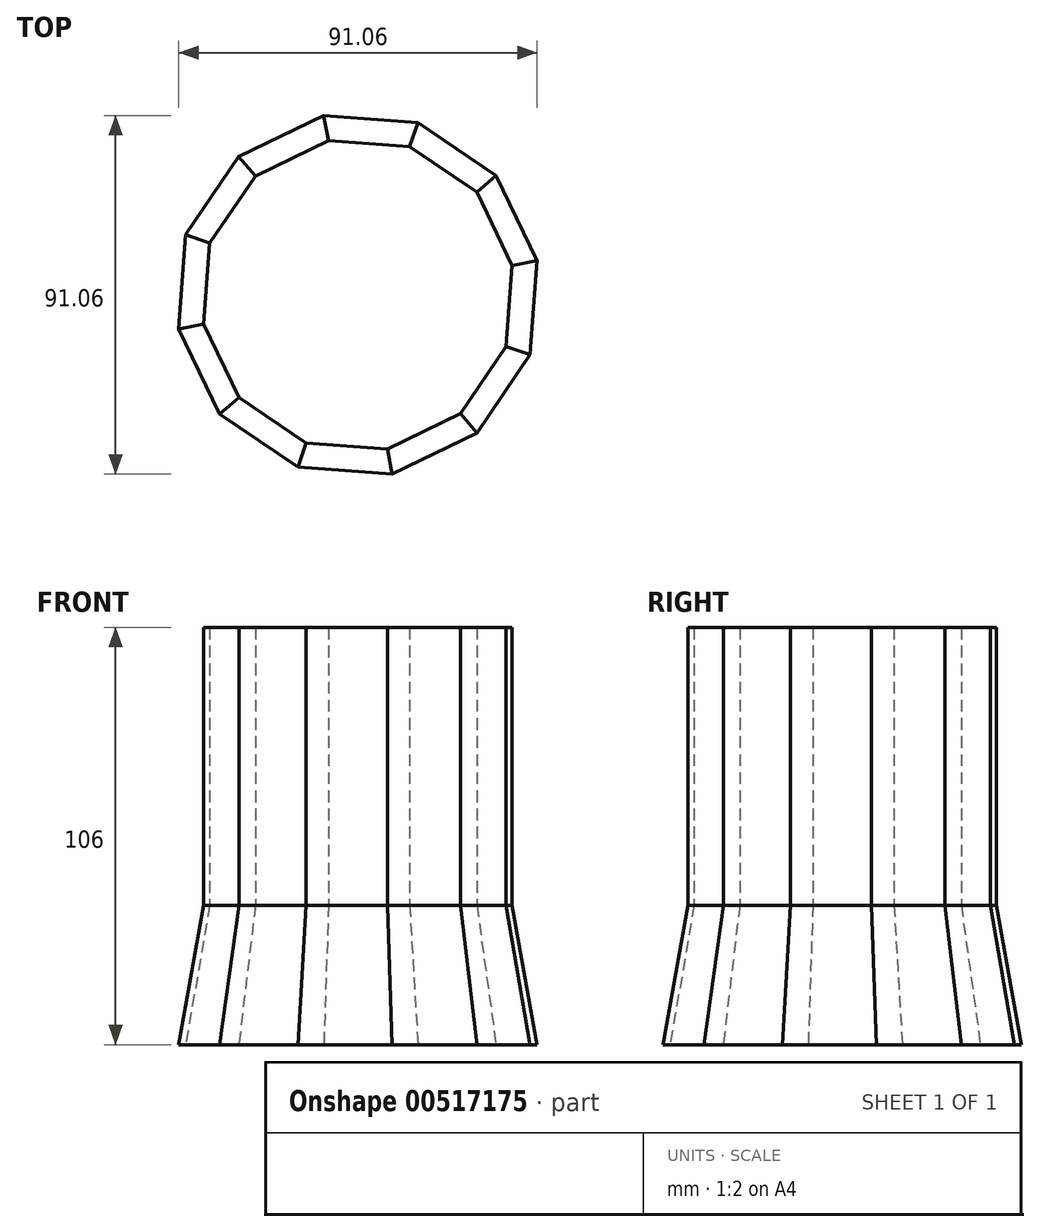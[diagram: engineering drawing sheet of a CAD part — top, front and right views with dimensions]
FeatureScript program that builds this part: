
annotation { "Feature Type Name" : "Feature", "Feature Type Description" : "" }
export const myFeature = defineFeature(function(context is Context, id is Id, definition is map)
    precondition{}
    {
        {
            var Q0;
            Q0=qCreatedBy(makeId("Top.planeOp"),FACE);
            var sketch = newSketch(context, id + "F0", { "sketchPlane" : qUnion([Q0])});
            skCircle(sketch, "E0.cCircle", {"center": v(0, 0) * mm, "radius": 44.77 * mm, "construction": true});
            skLineSegment(sketch, "E0.0", {"start": v(-43.77, 15.26) * mm, "end": v(-30.28, 35.1) * mm});
            skLineSegment(sketch, "E0.1", {"start": v(-30.28, 35.1) * mm, "end": v(-8.67, 45.53) * mm});
            skLineSegment(sketch, "E0.2", {"start": v(-8.67, 45.53) * mm, "end": v(15.26, 43.77) * mm});
            skLineSegment(sketch, "E0.3", {"start": v(15.26, 43.77) * mm, "end": v(35.1, 30.28) * mm});
            skLineSegment(sketch, "E0.4", {"start": v(35.1, 30.28) * mm, "end": v(45.53, 8.67) * mm});
            skLineSegment(sketch, "E0.5", {"start": v(45.53, 8.67) * mm, "end": v(43.77, -15.26) * mm});
            skLineSegment(sketch, "E0.6", {"start": v(43.77, -15.26) * mm, "end": v(30.28, -35.1) * mm});
            skLineSegment(sketch, "E0.7", {"start": v(30.28, -35.1) * mm, "end": v(8.67, -45.53) * mm});
            skLineSegment(sketch, "E0.8", {"start": v(8.67, -45.53) * mm, "end": v(-15.26, -43.77) * mm});
            skLineSegment(sketch, "E0.9", {"start": v(-15.26, -43.77) * mm, "end": v(-35.1, -30.28) * mm});
            skLineSegment(sketch, "E0.10", {"start": v(-35.1, -30.28) * mm, "end": v(-45.53, -8.67) * mm});
            skLineSegment(sketch, "E0.11", {"start": v(-45.53, -8.67) * mm, "end": v(-43.77, 15.26) * mm});
            skPoint(sketch, "E0.0.midPoint", {"position": v(-37.02, 25.17) * mm});
            skSolve(sketch);
        }
        {
            var Q0;
            Q0=makeQuery(id+"F0.imprint","IMPRINT",FACE,{"disambiguationData":[TD([[makeQuery(id+"F0.imprint","IMPRINT",EDGE,{"derivedFrom":sQuery(id+"F0.wireOp",EDGE,"E0.0")}),-1.0]])]});
            extrude(context, id + "F1", {"entities" : qUnion([Q0]), "depth" : 35.4 * mm, "offsetDistance" : 25 * mm, "hasDraft" : true, "draftAngle" : 10 * degree, "draftPullDirection" : true});
        }
        {
            var Q0;
            Q0=makeQuery(id+"F1.opExtrude","CAP_FACE",FACE,{"disambiguationData":[OSD([sQuery(id+"F0.wireOp",EDGE,"E0.0"),sQuery(id+"F0.wireOp",EDGE,"E0.1"),sQuery(id+"F0.wireOp",EDGE,"E0.2"),sQuery(id+"F0.wireOp",EDGE,"E0.3"),sQuery(id+"F0.wireOp",EDGE,"E0.4"),sQuery(id+"F0.wireOp",EDGE,"E0.5"),sQuery(id+"F0.wireOp",EDGE,"E0.6"),sQuery(id+"F0.wireOp",EDGE,"E0.7"),sQuery(id+"F0.wireOp",EDGE,"E0.8"),sQuery(id+"F0.wireOp",EDGE,"E0.9"),sQuery(id+"F0.wireOp",EDGE,"E0.10"),sQuery(id+"F0.wireOp",EDGE,"E0.11")])],"isStart":false});
            extrude(context, id + "F2", {"entities" : qUnion([Q0]), "operationType" : NewBodyOperationType.ADD, "depth" : 70.6 * mm, "offsetDistance" : 25 * mm});
        }
    });
